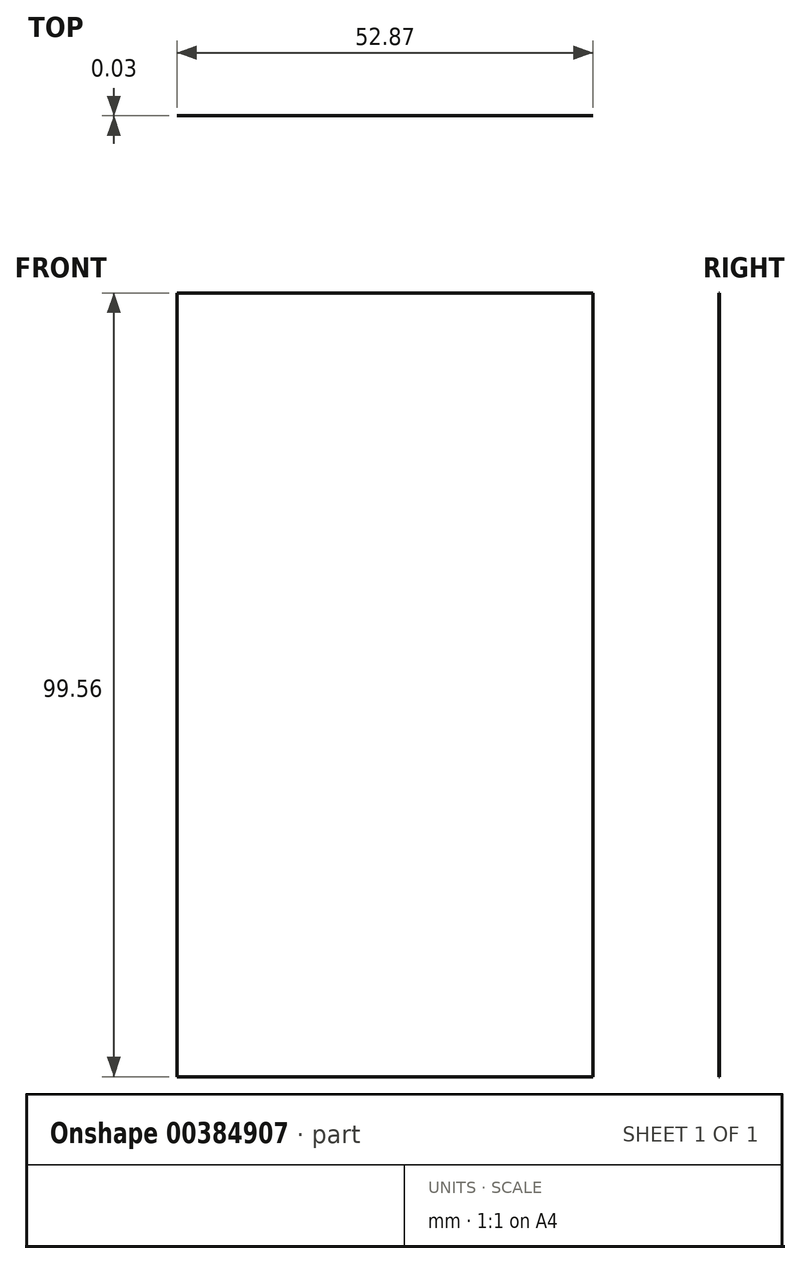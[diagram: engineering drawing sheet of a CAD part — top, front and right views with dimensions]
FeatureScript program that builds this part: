
annotation { "Feature Type Name" : "Feature", "Feature Type Description" : "" }
export const myFeature = defineFeature(function(context is Context, id is Id, definition is map)
    precondition{}
    {
        {
            var Q0;
            Q0=qCreatedBy(makeId("Front.planeOp"),FACE);
            var sketch = newSketch(context, id + "F0", { "sketchPlane" : qUnion([Q0])});
            skLineSegment(sketch, "E0.bottom", {"start": v(-63.56, 54.7) * mm, "end": v(-10.69, 54.7) * mm});
            skLineSegment(sketch, "E0.top", {"start": v(-63.56, -44.86) * mm, "end": v(-10.69, -44.86) * mm});
            skLineSegment(sketch, "E0.left", {"start": v(-63.56, 54.7) * mm, "end": v(-63.56, -44.86) * mm});
            skLineSegment(sketch, "E0.right", {"start": v(-10.69, 54.7) * mm, "end": v(-10.69, -44.86) * mm});
            skSolve(sketch);
        }
        {
            var Q0;
            Q0 = qSketchRegion(id + "F0", true);
            extrude(context, id + "F1", {"entities" : qUnion([Q0]), "depth" : 3 / 101.6 * mm});
        }
    });
